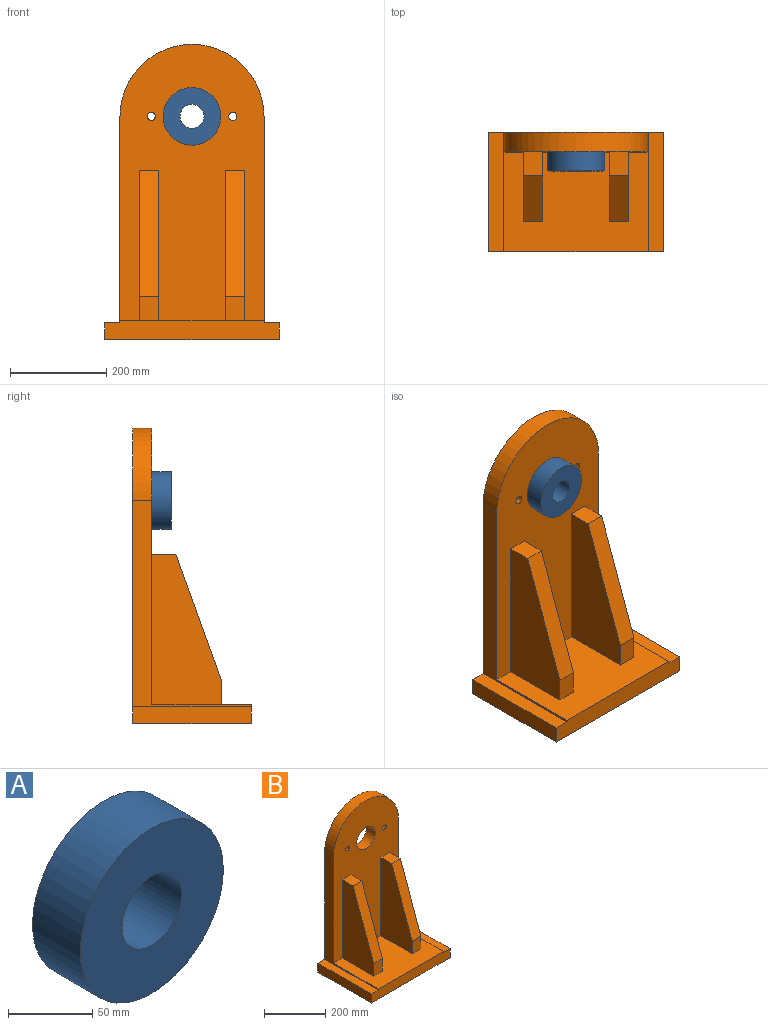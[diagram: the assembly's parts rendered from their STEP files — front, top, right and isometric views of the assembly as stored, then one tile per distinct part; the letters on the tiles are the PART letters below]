
ASSEMBLY  parts=2 mates=1
PART A: 4 faces, bbox 120x40x120 mm
  f0: cylinder r=25mm len=50mm, axis (0,1,0), area 6283.2mm2, adj f2,f3
  f1: cylinder r=60mm len=120mm, axis (0,1,0), area 15079.6mm2, adj f2,f3
  f2: plane 120x120mm, normal (0,-1,0), area 9346.2mm2, adj f0,f1
  f3: plane 120x120mm, normal (0,1,0), area 9346.2mm2, adj f0,f1
PART B: 25 faces, bbox 363x247x615 mm
  f0: plane 50x40mm, normal (0,-1,0), area 2000mm2, adj f3,f18,f20,f24
  f1: plane 50x40mm, normal (0,-1,0), area 2000mm2, adj f3,f21,f22,f23
  f2: plane 50x40mm, normal (0,0,1), area 2000mm2, adj f17,f21,f22,f23
  f3: plane 300x207mm, normal (0,0,1), area 50500mm2, adj f0,f1,f4,f10,f11,f17,f18,f20
  f4: plane 429.6x247mm, normal (-1,0,0), area 18136.2mm2, adj f3,f5,f11,f12,f13,f17
  f5: plane 247x31.5mm, normal (0,0,1), area 7780.5mm2, adj f4,f6,f11,f12
  f6: plane 247x35.4mm, normal (-1,0,0), area 8743.8mm2, adj f5,f7,f11,f12
  f7: plane 363x247mm, normal (0,0,-1), area 89661mm2, adj f6,f8,f11,f12
  f8: plane 247x35.4mm, normal (1,0,0), area 8743.8mm2, adj f7,f9,f11,f12
  f9: plane 247x31.5mm, normal (0,0,1), area 7780.5mm2, adj f8,f10,f11,f12
  f10: plane 429.6x247mm, normal (1,0,0), area 18136.2mm2, adj f3,f9,f11,f12,f13,f17
  f11: plane 363x40mm, normal (0,-1,0), area 14230.2mm2, adj f3,f4,f5,f6,f7,f8,f9,f10
  f12: plane 615x363mm, normal (0,1,0), area 170944.7mm2, adj f4,f5,f6,f7,f8,f9,f10,f13
  f13: cylinder r=150mm len=300mm, axis (0,1,0), area 18849.6mm2, adj f4,f10,f12,f17
  f14: cylinder r=42.5mm len=85mm, axis (0,1,0), area 10681.4mm2, adj f12,f17
  f15: cylinder r=8.5mm len=40mm, axis (0,1,0), area 2136.3mm2, adj f12,f17
  f16: cylinder r=8.5mm len=40mm, axis (0,1,0), area 2136.3mm2, adj f12,f17
  f17: plane 575x300mm, normal (0,-1,0), area 131674.5mm2, adj f2,f3,f4,f10,f13,f14,f15,f16
  f18: plane 313x145mm, normal (1,0,0), area 32892.5mm2, adj f0,f3,f17,f19,f24
  f19: plane 50x40mm, normal (0,0,1), area 2000mm2, adj f17,f18,f20,f24
  f20: plane 313x145mm, normal (-1,0,0), area 32892.5mm2, adj f0,f3,f17,f19,f24
  f21: plane 313x145mm, normal (1,0,0), area 32892.5mm2, adj f1,f2,f3,f17,f23
  f22: plane 313x145mm, normal (-1,0,0), area 32892.5mm2, adj f1,f2,f3,f17,f23
  f23: plane 263x95mm, normal (0,-0.94,0.34), area 11185.3mm2, adj f1,f2,f21,f22
  f24: plane 263x95mm, normal (0,-0.94,0.34), area 11185.3mm2, adj f0,f18,f19,f20
PLACE A t=(-398.72,-86,556.37)mm
PLACE B t=(-217.22,-46,91.37)mm
MATE fastened A.f0 <-> B.f13  axis (0,1,0) through (-398.72,-86,556.37)mm
